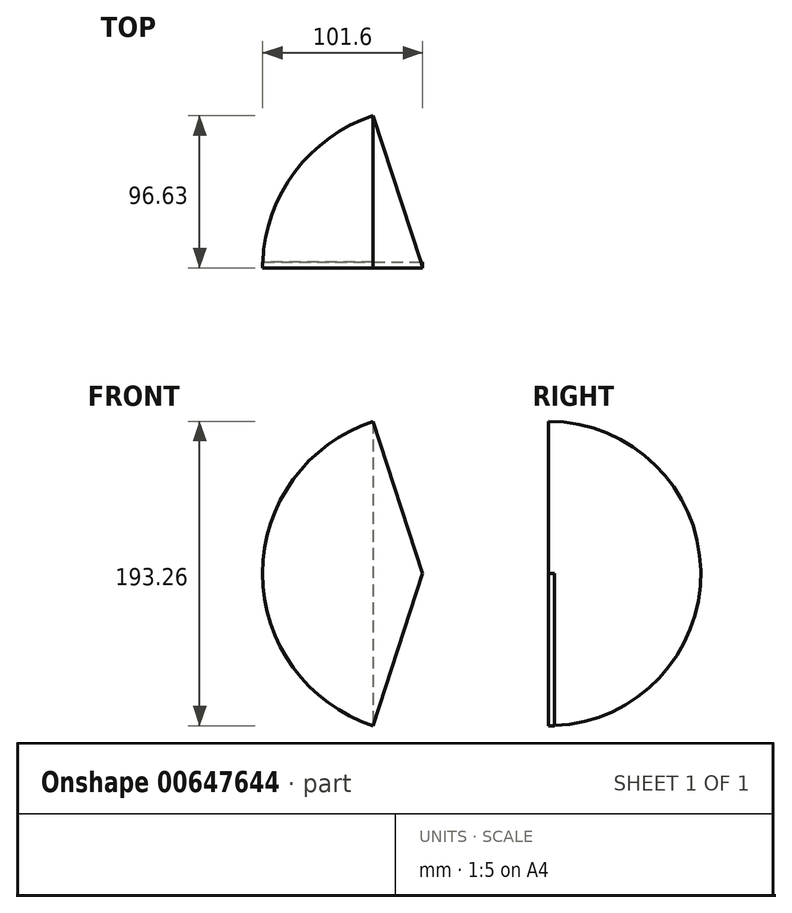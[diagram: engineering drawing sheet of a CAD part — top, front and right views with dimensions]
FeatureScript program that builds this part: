
annotation { "Feature Type Name" : "Feature", "Feature Type Description" : "" }
export const myFeature = defineFeature(function(context is Context, id is Id, definition is map)
    precondition{}
    {
        {
            var Q0;
            Q0=qCreatedBy(makeId("Top.planeOp"),FACE);
            var sketch = newSketch(context, id + "F0", { "sketchPlane" : qUnion([Q0])});
            skLineSegment(sketch, "E0.bottom", {"start": v(-101.6, -3.67) * mm, "end": v(0, -3.67) * mm});
            skLineSegment(sketch, "E0.top", {"start": v(-101.6, 0) * mm, "end": v(0, 0) * mm});
            skLineSegment(sketch, "E0.left", {"start": v(-101.6, 0) * mm, "end": v(-101.6, -3.67) * mm});
            skLineSegment(sketch, "E0.right", {"start": v(0, 0) * mm, "end": v(0, -3.67) * mm});
            skSolve(sketch);
        }
        {
            var Q0;
            Q0 = qSketchRegion(id + "F0", true);
            var Q1;
            Q1=sQuery(id+"F0.wireOp",EDGE,"E0.right");
            revolve(context, id + "F1", {"entities" : qUnion([Q0]), "axis" : qUnion([Q1]), "revolveType" : RevolveType.ONE_DIRECTION, "angle" : 72 * degree});
        }
        {
            var Q0;
            Q0=makeQuery(id+"F1.opRevolve","SWEPT_FACE",FACE,{"disambiguationData":[OSD([sQuery(id+"F0.wireOp",EDGE,"E0.bottom")])]});
            var Q1;
            Q1=sQuery(id+"F0.wireOp",EDGE,"E0.bottom");
            revolve(context, id + "F2", {"operationType" : NewBodyOperationType.ADD, "entities" : qUnion([Q0]), "axis" : qUnion([Q1]), "revolveType" : RevolveType.ONE_DIRECTION, "angle" : 180 * degree});
        }
    });
